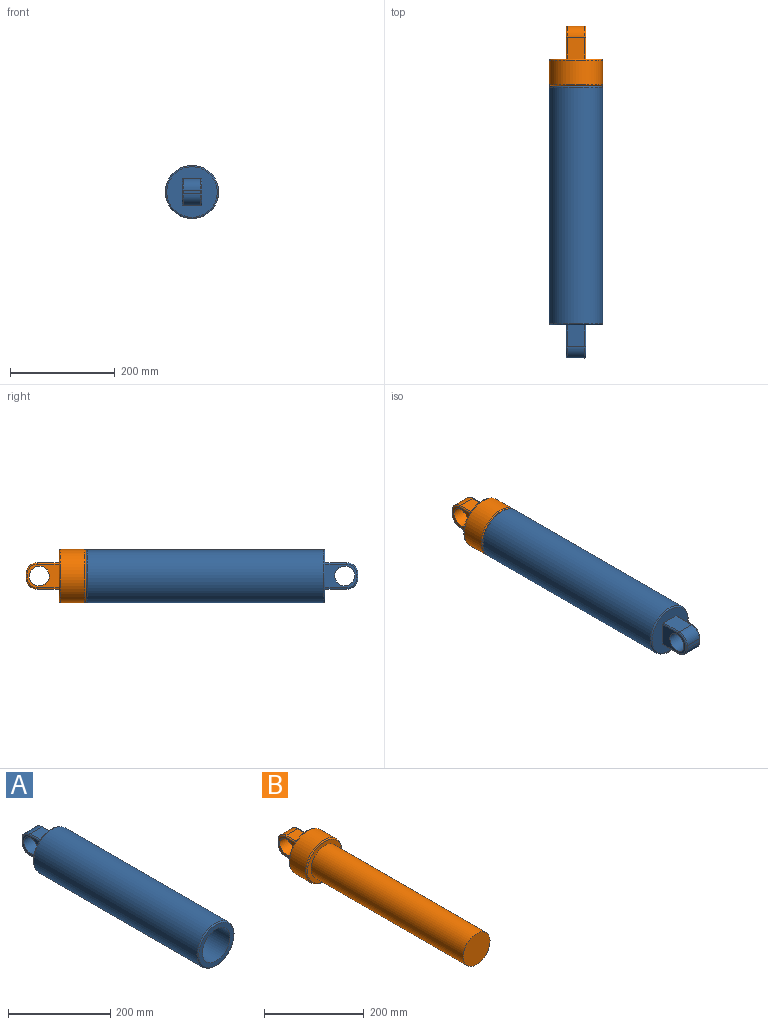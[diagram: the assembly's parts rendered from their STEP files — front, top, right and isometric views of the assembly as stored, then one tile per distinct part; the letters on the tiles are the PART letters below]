
ASSEMBLY  parts=2 mates=1
PART A: 25 faces, bbox 110x522.5x110 mm
  f0: cylinder r=50.8mm len=452.12mm, axis (0,1,0), area 144310.3mm2, adj f23,f24
  f1: plane 96.52x96.52mm, normal (0,-1,0), area 2756.5mm2, adj f4,f24
  f2: plane 96.52x96.52mm, normal (0,1,0), area 5386.9mm2, adj f5,f6,f7,f8,f13,f17,f18,f22
  f3: cone r=0mm half-angle=59deg, axis (0,-1,0), area 5320.3mm2, adj f4
  f4: cylinder r=38.1mm len=431.8mm, axis (0,-1,0), area 103368.3mm2, adj f1,f3
  f5: plane 41.91x33.02mm, normal (0,0,-1), area 1383.9mm2, adj f2,f12,f17,f22
  f6: plane 60.96x45.72mm, normal (-1,0,0), area 1491.2mm2, adj f2,f10,f18,f19,f20,f21,f22
  f7: plane 41.91x33.02mm, normal (0,0,1), area 1383.9mm2, adj f2,f11,f13,f18
  f8: plane 60.96x45.72mm, normal (1,0,0), area 1491.2mm2, adj f2,f10,f13,f14,f15,f16,f17
  f9: plane 33.02x7.62mm, normal (0,1,0), area 251.6mm2, adj f11,f12,f15,f20
  f10: cylinder r=19.05mm len=38.1mm, axis (-1,0,0), area 4560.4mm2, adj f6,f8
  f11: cylinder r=21.59mm len=33.02mm, axis (-1,0,0), area 1119.8mm2, adj f7,f9,f14,f19
  f12: cylinder r=21.59mm len=33.02mm, axis (1,0,0), area 1119.8mm2, adj f5,f9,f16,f21
  f13: cylinder r=2.54mm len=41.91mm, axis (0,1,0), area 167.2mm2, adj f2,f7,f8,f14
  f14: torus R=19.05mm, axis (1,0,0), area 129.5mm2, adj f8,f11,f13,f15
  f15: cylinder r=2.54mm len=7.62mm, axis (0,0,1), area 30.4mm2, adj f8,f9,f14,f16
  f16: torus R=19.05mm, axis (1,0,0), area 129.5mm2, adj f8,f12,f15,f17
  f17: cylinder r=2.54mm len=41.91mm, axis (0,-1,0), area 167.2mm2, adj f2,f5,f8,f16
  f18: cylinder r=2.54mm len=41.91mm, axis (0,-1,0), area 167.2mm2, adj f2,f6,f7,f19
  f19: torus R=19.05mm, axis (1,0,0), area 129.5mm2, adj f6,f11,f18,f20
  f20: cylinder r=2.54mm len=7.62mm, axis (0,0,-1), area 30.4mm2, adj f6,f9,f19,f21
  f21: torus R=19.05mm, axis (1,0,0), area 129.5mm2, adj f6,f12,f20,f22
  f22: cylinder r=2.54mm len=41.91mm, axis (0,1,0), area 167.2mm2, adj f2,f5,f6,f21
  f23: torus R=48.26mm, axis (0,-1,0), area 1250.4mm2, adj f0,f2
  f24: torus R=48.26mm, axis (0,-1,0), area 1250.4mm2, adj f0,f1
PART B: 25 faces, bbox 110x547.9x110 mm
  f0: cylinder r=50.8mm len=101.6mm, axis (0,1,0), area 14593.2mm2, adj f18,f19
  f1: plane 96.52x96.52mm, normal (0,-1,0), area 2756.5mm2, adj f3,f19
  f2: plane 96.52x96.52mm, normal (0,1,0), area 5386.9mm2, adj f5,f6,f7,f8,f13,f17,f18,f20
  f3: cylinder r=38.1mm len=431.8mm, axis (0,1,0), area 103368.3mm2, adj f1,f4
  f4: plane 76.2x76.2mm, normal (0,-1,0), area 4560.4mm2, adj f3
  f5: plane 41.91x33.02mm, normal (0,0,-1), area 1383.9mm2, adj f2,f12,f17,f20
  f6: plane 60.96x45.72mm, normal (-1,0,0), area 1491.2mm2, adj f2,f10,f13,f14,f15,f16,f17
  f7: plane 41.91x33.02mm, normal (0,0,1), area 1383.9mm2, adj f2,f11,f13,f24
  f8: plane 60.96x45.72mm, normal (1,0,0), area 1491.2mm2, adj f2,f10,f20,f21,f22,f23,f24
  f9: plane 33.02x7.62mm, normal (0,1,0), area 251.6mm2, adj f11,f12,f15,f22
  f10: cylinder r=19.05mm len=38.1mm, axis (-1,0,0), area 4560.4mm2, adj f6,f8
  f11: cylinder r=21.59mm len=33.02mm, axis (-1,0,0), area 1119.8mm2, adj f7,f9,f14,f23
  f12: cylinder r=21.59mm len=33.02mm, axis (1,0,0), area 1119.8mm2, adj f5,f9,f16,f21
  f13: cylinder r=2.54mm len=41.91mm, axis (0,-1,0), area 167.2mm2, adj f2,f6,f7,f14
  f14: torus R=19.05mm, axis (1,0,0), area 129.5mm2, adj f6,f11,f13,f15
  f15: cylinder r=2.54mm len=7.62mm, axis (0,0,-1), area 30.4mm2, adj f6,f9,f14,f16
  f16: torus R=19.05mm, axis (1,0,0), area 129.5mm2, adj f6,f12,f15,f17
  f17: cylinder r=2.54mm len=41.91mm, axis (0,1,0), area 167.2mm2, adj f2,f5,f6,f16
  f18: torus R=48.26mm, axis (0,-1,0), area 1250.4mm2, adj f0,f2
  f19: torus R=48.26mm, axis (0,-1,0), area 1250.4mm2, adj f0,f1
  f20: cylinder r=2.54mm len=41.91mm, axis (0,-1,0), area 167.2mm2, adj f2,f5,f8,f21
  f21: torus R=19.05mm, axis (1,0,0), area 129.5mm2, adj f8,f12,f20,f22
  f22: cylinder r=2.54mm len=7.62mm, axis (0,0,1), area 30.4mm2, adj f8,f9,f21,f23
  f23: torus R=19.05mm, axis (1,0,0), area 129.5mm2, adj f8,f11,f22,f24
  f24: cylinder r=2.54mm len=41.91mm, axis (0,1,0), area 167.2mm2, adj f2,f7,f8,f23
PLACE A rot(axis=(0,0,-1),180deg) t=(255.5,-257.71,538.58)mm fixed
PLACE B rot(axis=(0,-1,0),180deg) t=(255.5,250.29,538.58)mm
MATE slider A.f3 <-> B.f3  axis (0,1,0) through (255.5,199.49,538.58)mm
